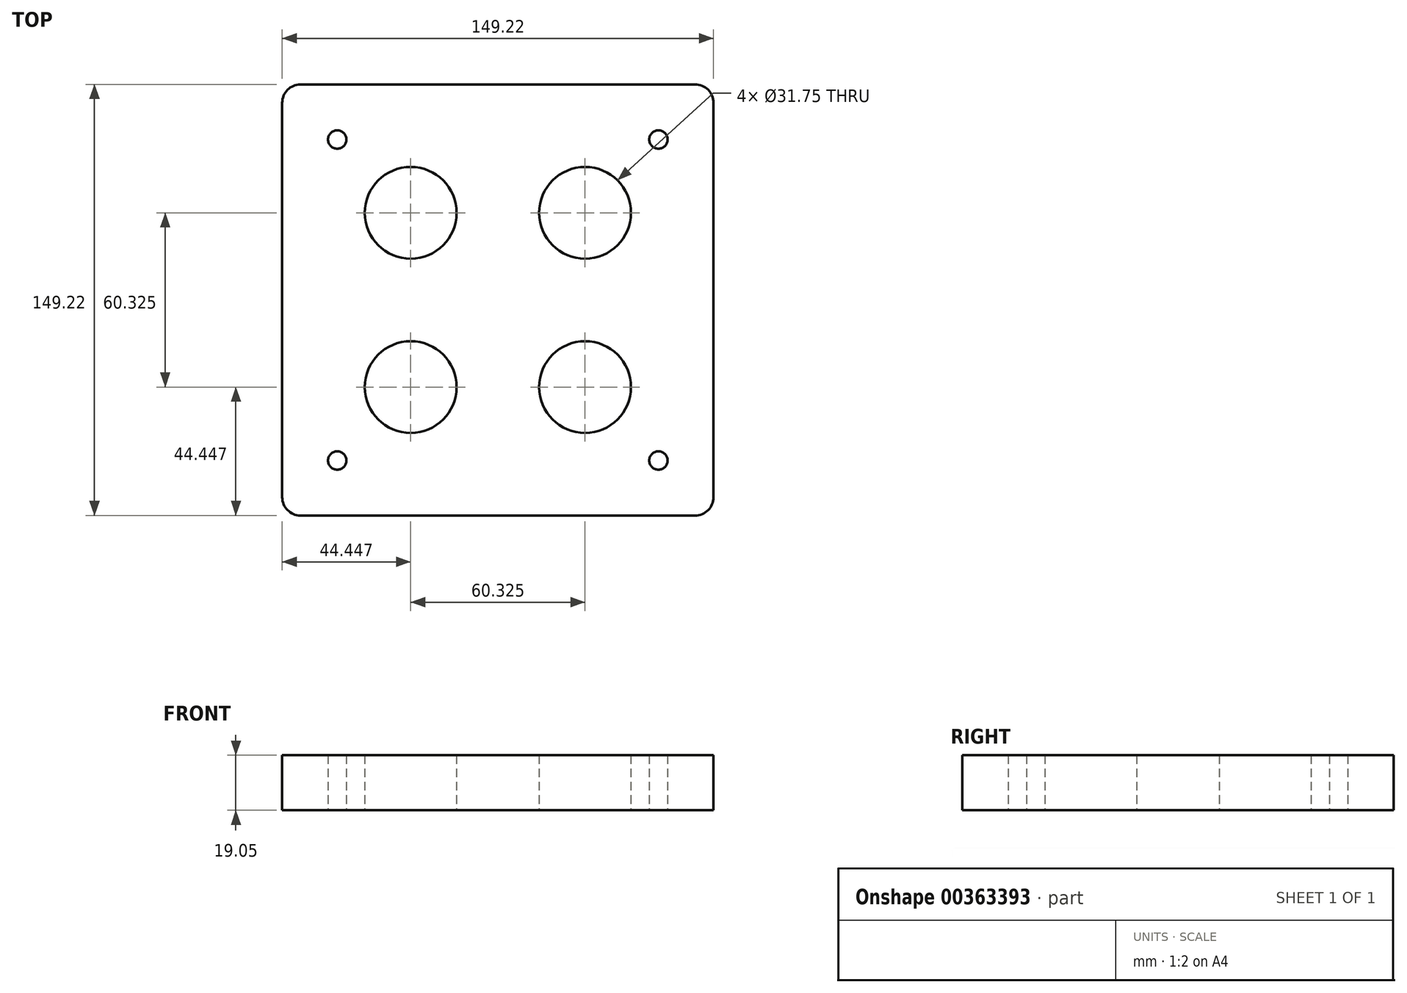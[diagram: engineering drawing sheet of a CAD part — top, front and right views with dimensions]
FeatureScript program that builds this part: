
annotation { "Feature Type Name" : "Feature", "Feature Type Description" : "" }
export const myFeature = defineFeature(function(context is Context, id is Id, definition is map)
    precondition{}
    {
        {
            var Q0;
            Q0=qCreatedBy(makeId("Top.planeOp"),FACE);
            var sketch = newSketch(context, id + "F0", { "sketchPlane" : qUnion([Q0])});
            skLineSegment(sketch, "E0.bottom", {"start": v(-74.61, 74.61) * mm, "end": v(74.61, 74.61) * mm});
            skLineSegment(sketch, "E0.top", {"start": v(-74.61, -74.61) * mm, "end": v(74.61, -74.61) * mm});
            skLineSegment(sketch, "E0.left", {"start": v(-74.61, 74.61) * mm, "end": v(-74.61, -74.61) * mm});
            skLineSegment(sketch, "E0.right", {"start": v(74.61, 74.61) * mm, "end": v(74.61, -74.61) * mm});
            skPoint(sketch, "E0.middle", {"position": v(0, 0) * mm});
            skCircle(sketch, "E1", {"center": v(-30.16, 30.16) * mm, "radius": 15.88 * mm});
            skCircle(sketch, "E2", {"center": v(30.16, 30.16) * mm, "radius": 15.88 * mm});
            skCircle(sketch, "E3", {"center": v(30.16, -30.16) * mm, "radius": 15.88 * mm});
            skCircle(sketch, "E4", {"center": v(-30.16, -30.16) * mm, "radius": 15.88 * mm});
            skCircle(sketch, "E5", {"center": v(-55.56, -55.56) * mm, "radius": 3.18 * mm});
            skCircle(sketch, "E6", {"center": v(-55.56, 55.56) * mm, "radius": 3.18 * mm});
            skCircle(sketch, "E7", {"center": v(55.56, 55.56) * mm, "radius": 3.18 * mm});
            skCircle(sketch, "E8", {"center": v(55.56, -55.56) * mm, "radius": 3.18 * mm});
            skSolve(sketch);
        }
        {
            var Q0;
            Q0=makeQuery(id+"F0.imprint","IMPRINT",FACE,{"disambiguationData":[TD([[makeQuery(id+"F0.imprint","IMPRINT",EDGE,{"derivedFrom":sQuery(id+"F0.wireOp",EDGE,"E0.bottom")}),-1.0]])]});
            extrude(context, id + "F1", {"entities" : qUnion([Q0]), "depth" : 19.05 * mm});
        }
        {
            var Q0;
            Q0=makeQuery(id+"F1.opExtrude","SWEPT_EDGE",EDGE,{"disambiguationData":[OSD([sQuery(id+"F0.wireOp",EDGE,"E0.bottom"),sQuery(id+"F0.wireOp",EDGE,"E0.left")])]});
            var Q1;
            Q1=makeQuery(id+"F1.opExtrude","SWEPT_EDGE",EDGE,{"disambiguationData":[OSD([sQuery(id+"F0.wireOp",EDGE,"E0.bottom"),sQuery(id+"F0.wireOp",EDGE,"E0.right")])]});
            var Q2;
            Q2=makeQuery(id+"F1.opExtrude","SWEPT_EDGE",EDGE,{"disambiguationData":[OSD([sQuery(id+"F0.wireOp",EDGE,"E0.top"),sQuery(id+"F0.wireOp",EDGE,"E0.right")])]});
            var Q3;
            Q3=makeQuery(id+"F1.opExtrude","SWEPT_EDGE",EDGE,{"disambiguationData":[OSD([sQuery(id+"F0.wireOp",EDGE,"E0.top"),sQuery(id+"F0.wireOp",EDGE,"E0.left")])]});
            fillet(context, id + "F2", {"entities" : qUnion([Q0, Q1, Q2, Q3]), "radius" : 6.35 * mm, "tangentPropagation" : true, "allowEdgeOverflow" : false});
        }
    });
